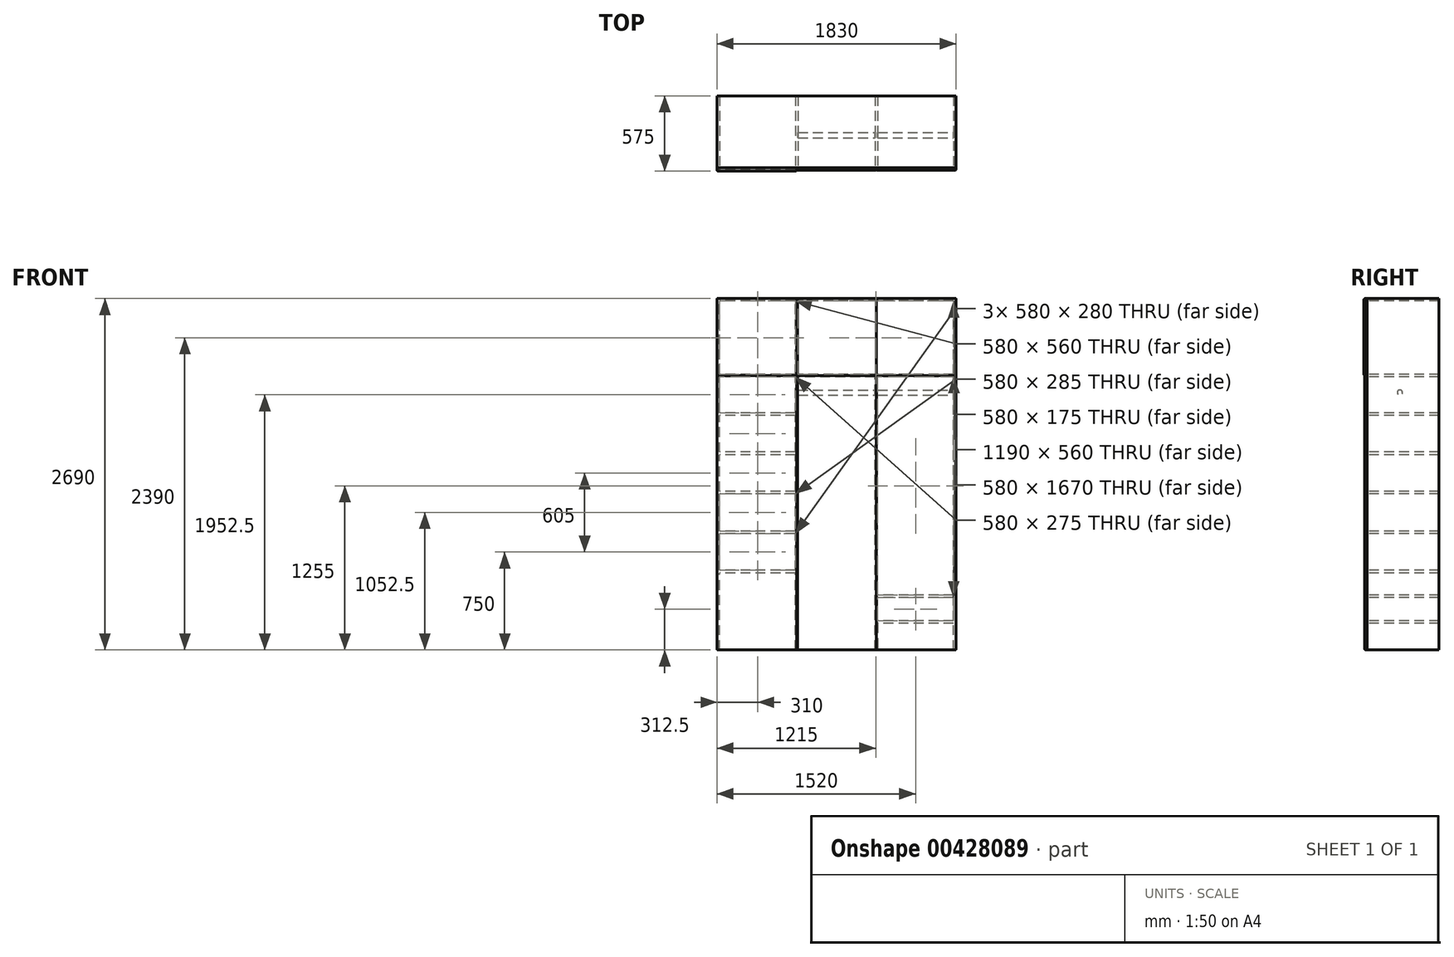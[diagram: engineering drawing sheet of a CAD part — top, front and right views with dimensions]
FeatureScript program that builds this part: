
annotation { "Feature Type Name" : "Feature", "Feature Type Description" : "" }
export const myFeature = defineFeature(function(context is Context, id is Id, definition is map)
    precondition{}
    {
        {
            var Q0;
            Q0=qCreatedBy(makeId("Front.planeOp"),FACE);
            var sketch = newSketch(context, id + "F0", { "sketchPlane" : qUnion([Q0])});
            skLineSegment(sketch, "E0.bottom", {"start": v(915, -1345) * mm, "end": v(-915, -1345) * mm});
            skLineSegment(sketch, "E0.top", {"start": v(915, 1345) * mm, "end": v(-915, 1345) * mm});
            skLineSegment(sketch, "E0.left", {"start": v(915, -1345) * mm, "end": v(915, 1345) * mm});
            skLineSegment(sketch, "E0.right", {"start": v(-915, -1345) * mm, "end": v(-915, 1345) * mm});
            skPoint(sketch, "E0.middle", {"position": v(0, 0) * mm});
            skLineSegment(sketch, "E1.0", {"start": v(895, 745) * mm, "end": v(315, 745) * mm});
            skLineSegment(sketch, "E2.trimOffspring", {"start": v(-315, 745) * mm, "end": v(-895, 745) * mm});
            skLineSegment(sketch, "E3", {"start": v(295, 745) * mm, "end": v(-295, 745) * mm});
            skLineSegment(sketch, "E4.0", {"start": v(-315, 470) * mm, "end": v(-895, 470) * mm});
            skLineSegment(sketch, "E5.0", {"start": v(-315, 170) * mm, "end": v(-895, 170) * mm});
            skLineSegment(sketch, "E6.0", {"start": v(-315, -130) * mm, "end": v(-895, -130) * mm});
            skLineSegment(sketch, "E7.0", {"start": v(-315, -455) * mm, "end": v(-895, -455) * mm});
            skLineSegment(sketch, "E8.0", {"start": v(-315, -755) * mm, "end": v(-895, -755) * mm});
            skLineSegment(sketch, "E9.0", {"start": v(895, -945) * mm, "end": v(315, -945) * mm});
            skLineSegment(sketch, "E10.0", {"start": v(295, 645) * mm, "end": v(-295, 645) * mm});
            skLineSegment(sketch, "E11.0", {"start": v(295, 625) * mm, "end": v(-295, 625) * mm});
            skLineSegment(sketch, "E12.0", {"start": v(295, -375) * mm, "end": v(-295, -375) * mm});
            skLineSegment(sketch, "E13.0", {"start": v(295, -395) * mm, "end": v(-295, -395) * mm});
            skLineSegment(sketch, "E14", {"start": v(315, 645) * mm, "end": v(895, 645) * mm});
            skLineSegment(sketch, "E15", {"start": v(315, 625) * mm, "end": v(895, 625) * mm});
            skLineSegment(sketch, "E16.0", {"start": v(895, -1120) * mm, "end": v(315, -1120) * mm});
            skLineSegment(sketch, "E17.0", {"start": v(-895, -1345) * mm, "end": v(-895, -755) * mm});
            skLineSegment(sketch, "E18.0", {"start": v(895, 1325) * mm, "end": v(-295, 1325) * mm});
            skLineSegment(sketch, "E19.0", {"start": v(895, -1320) * mm, "end": v(895, -1140) * mm});
            skLineSegment(sketch, "E20.0", {"start": v(-315, 765) * mm, "end": v(-895, 765) * mm});
            skLineSegment(sketch, "E20.1", {"start": v(295, 765) * mm, "end": v(-295, 765) * mm});
            skLineSegment(sketch, "E20.2", {"start": v(895, 765) * mm, "end": v(315, 765) * mm});
            skLineSegment(sketch, "E21.0", {"start": v(-315, 450) * mm, "end": v(-895, 450) * mm});
            skLineSegment(sketch, "E22.0", {"start": v(-315, 150) * mm, "end": v(-895, 150) * mm});
            skLineSegment(sketch, "E23.0", {"start": v(-315, -150) * mm, "end": v(-895, -150) * mm});
            skLineSegment(sketch, "E24.0", {"start": v(-315, -435) * mm, "end": v(-895, -435) * mm});
            skLineSegment(sketch, "E25.0", {"start": v(-315, -735) * mm, "end": v(-895, -735) * mm});
            skLineSegment(sketch, "E26.0", {"start": v(895, -925) * mm, "end": v(315, -925) * mm});
            skLineSegment(sketch, "E27.0", {"start": v(895, -1140) * mm, "end": v(315, -1140) * mm});
            skLineSegment(sketch, "E28.0", {"start": v(295, -1345) * mm, "end": v(295, 745) * mm});
            skLineSegment(sketch, "E29.0", {"start": v(315, -1320) * mm, "end": v(315, -1140) * mm});
            skLineSegment(sketch, "E30.0", {"start": v(-295, -1345) * mm, "end": v(-295, 745) * mm});
            skLineSegment(sketch, "E31.0", {"start": v(-315, -1345) * mm, "end": v(-315, -755) * mm});
            skLineSegment(sketch, "E32.trimOffspring", {"start": v(-315, 1325) * mm, "end": v(-895, 1325) * mm});
            skLineSegment(sketch, "E33.trimOffspring", {"start": v(895, 765) * mm, "end": v(895, 1325) * mm});
            skLineSegment(sketch, "E34.trimOffspring", {"start": v(-295, 765) * mm, "end": v(-295, 1325) * mm});
            skLineSegment(sketch, "E35.trimOffspring", {"start": v(-315, 765) * mm, "end": v(-315, 1325) * mm});
            skLineSegment(sketch, "E36.trimOffspring", {"start": v(-895, 765) * mm, "end": v(-895, 1325) * mm});
            skLineSegment(sketch, "E37.trimOffspring", {"start": v(-895, 470) * mm, "end": v(-895, 745) * mm});
            skLineSegment(sketch, "E38.trimOffspring", {"start": v(-315, 470) * mm, "end": v(-315, 745) * mm});
            skLineSegment(sketch, "E39.trimOffspring", {"start": v(-895, 170) * mm, "end": v(-895, 450) * mm});
            skLineSegment(sketch, "E40.trimOffspring", {"start": v(-895, -130) * mm, "end": v(-895, 150) * mm});
            skLineSegment(sketch, "E41.trimOffspring", {"start": v(-315, -130) * mm, "end": v(-315, 150) * mm});
            skLineSegment(sketch, "E42.trimOffspring", {"start": v(-315, 170) * mm, "end": v(-315, 450) * mm});
            skLineSegment(sketch, "E43.trimOffspring", {"start": v(-315, -435) * mm, "end": v(-315, -150) * mm});
            skLineSegment(sketch, "E44.trimOffspring", {"start": v(-895, -435) * mm, "end": v(-895, -150) * mm});
            skLineSegment(sketch, "E45.trimOffspring", {"start": v(-895, -735) * mm, "end": v(-895, -455) * mm});
            skPoint(sketch, "E46.orphan", {"position": v(-915, -755) * mm});
            skLineSegment(sketch, "E47.trimOffspring", {"start": v(-315, -735) * mm, "end": v(-315, -455) * mm});
            skLineSegment(sketch, "E48.trimOffspring", {"start": v(315, -925) * mm, "end": v(315, 745) * mm});
            skLineSegment(sketch, "E49.trimOffspring", {"start": v(895, -925) * mm, "end": v(895, 745) * mm});
            skPoint(sketch, "E50.orphan", {"position": v(915, -945) * mm});
            skLineSegment(sketch, "E51.trimOffspring", {"start": v(895, -1120) * mm, "end": v(895, -945) * mm});
            skLineSegment(sketch, "E52.trimOffspring", {"start": v(315, -1120) * mm, "end": v(315, -945) * mm});
            skLineSegment(sketch, "E53", {"start": v(315, 765) * mm, "end": v(295, 765) * mm});
            skLineSegment(sketch, "E54", {"start": v(315, -1320) * mm, "end": v(315, -1345) * mm});
            skLineSegment(sketch, "E55", {"start": v(895, -1320) * mm, "end": v(895, -1345) * mm});
            skSolve(sketch);
        }
        {
            var Q0;
            Q0=makeQuery(id+"F0.imprint","IMPRINT",FACE,{"disambiguationData":[TD([[makeQuery(id+"F0.imprint","IMPRINT",EDGE,{"derivedFrom":sQuery(id+"F0.wireOp",EDGE,"E0.top")}),1.0]])]});
            extrude(context, id + "F1", {"entities" : qUnion([Q0]), "oppositeDirection" : true, "depth" : 550 * mm});
        }
        {
            var Q0;
            {var subQ0=sQuery(id+"F0.wireOp",EDGE,"E10.0");Q0=makeQuery(id+"F0.imprint","IMPRINT",FACE,{"disambiguationData":[TD([[makeQuery(id+"F0.imprint","IMPRINT",EDGE,{"derivedFrom":subQ0}),1.0]])]});}
            var Q1;
            {var subQ0=sQuery(id+"F0.wireOp",EDGE,"E14");Q1=makeQuery(id+"F0.imprint","IMPRINT",FACE,{"disambiguationData":[TD([[makeQuery(id+"F0.imprint","IMPRINT",EDGE,{"derivedFrom":subQ0}),-1.0]])]});}
            var Q2;
            Q2=sQuery(id+"F0.wireOp",EDGE,"E11.0");
            revolve(context, id + "F2", {"entities" : qUnion([Q0, Q1]), "axis" : qUnion([Q2]), "revolveType" : RevolveType.FULL});
        }
        {
            var Q0;
            Q0=sQuery(id+"F0.wireOp",EDGE,"E12.0");
            var Q1;
            Q1=sQuery(id+"F0.wireOp",EDGE,"E13.0");
            revolve(context, id + "F3", {"bodyType" : ToolBodyType.SURFACE, "surfaceEntities" : qUnion([Q0]), "axis" : qUnion([Q1]), "revolveType" : RevolveType.FULL});
        }
        {
            var Q0;
            Q0=makeQuery(id+"F2.opRevolve","SWEPT_BODY",BODY,{"disambiguationData":[OSD([sQuery(id+"F0.wireOp",EDGE,"E10.0"),sQuery(id+"F0.wireOp",EDGE,"E11.0"),sQuery(id+"F0.wireOp",EDGE,"E28.0"),sQuery(id+"F0.wireOp",EDGE,"E30.0")])]});
            var Q1;
            Q1=makeQuery(id+"F2.opRevolve","SWEPT_BODY",BODY,{"disambiguationData":[OSD([sQuery(id+"F0.wireOp",EDGE,"E14"),sQuery(id+"F0.wireOp",EDGE,"E15"),sQuery(id+"F0.wireOp",EDGE,"E48.trimOffspring"),sQuery(id+"F0.wireOp",EDGE,"E49.trimOffspring")])]});
            var Q2;
            Q2=makeQuery(id+"F3.opRevolve","SWEPT_BODY",BODY,{"disambiguationData":[OSD([sQuery(id+"F0.wireOp",EDGE,"E12.0")])]});
            var Q3;
            Q3=makeQuery(id+"F1.opExtrude","SWEPT_EDGE",EDGE,{"disambiguationData":[OSD([sQuery(id+"F0.wireOp",EDGE,"E25.0"),sQuery(id+"F0.wireOp",EDGE,"E45.trimOffspring")])]});
            transform(context, id + "F4", {"entities" : qUnion([Q0, Q1, Q2]), "transformType" : TransformType.TRANSLATION_DISTANCE, "transformDirection" : qUnion([Q3]), "distance" : 250 * mm, "oppositeDirection" : true, "makeCopy" : false});
        }
        {
            var Q0;
            Q0=qCreatedBy(makeId("Front.planeOp"),FACE);
            var sketch = newSketch(context, id + "F5", { "sketchPlane" : qUnion([Q0])});
            skLineSegment(sketch, "E56.bottom", {"start": v(915, -1345) * mm, "end": v(-915, -1345) * mm});
            skLineSegment(sketch, "E56.top", {"start": v(915, 1345) * mm, "end": v(-915, 1345) * mm});
            skLineSegment(sketch, "E56.left", {"start": v(915, -1345) * mm, "end": v(915, 1345) * mm});
            skLineSegment(sketch, "E56.right", {"start": v(-915, -1345) * mm, "end": v(-915, 1345) * mm});
            skPoint(sketch, "E56.middle", {"position": v(0, 0) * mm});
            skLineSegment(sketch, "E57.0", {"start": v(305, -1345) * mm, "end": v(305, 1345) * mm});
            skLineSegment(sketch, "E58.0", {"start": v(-305, -1345) * mm, "end": v(-305, 1345) * mm});
            skLineSegment(sketch, "E59.0", {"start": v(-300, -1345) * mm, "end": v(-300, 1345) * mm});
            skLineSegment(sketch, "E60.0", {"start": v(915, 755) * mm, "end": v(-915, 755) * mm});
            skSolve(sketch);
        }
        {
            var Q0;
            {var subQ0=sQuery(id+"F5.wireOp",EDGE,"E56.right");var subQ1=sQuery(id+"F5.wireOp",EDGE,"E56.bottom");var subQ2=makeQuery(id+"F5.imprint","INTERSECT",VERTEX,{"derivedFrom":[subQ1,subQ0]});Q0=makeQuery(id+"F5.imprint","IMPRINT",FACE,{"disambiguationData":[TD([[makeQuery(id+"F5.imprint","IMPRINT",EDGE,{"disambiguationData":[TD([[subQ2,1.0]])],"derivedFrom":subQ1}),-1.0]])]});}
            extrude(context, id + "F6", {"entities" : qUnion([Q0]), "depth" : 20 * mm});
        }
        {
            var Q0;
            Q0=makeQuery(id+"F6.opExtrude","SWEPT_EDGE",EDGE,{"disambiguationData":[OSD([sQuery(id+"F5.wireOp",EDGE,"E58.0"),sQuery(id+"F5.wireOp",EDGE,"E60.0")])]});
            var Q1;
            Q1=makeQuery(id+"F6.opExtrude","SWEPT_EDGE",EDGE,{"disambiguationData":[OSD([sQuery(id+"F5.wireOp",EDGE,"E56.right"),sQuery(id+"F5.wireOp",EDGE,"E60.0")])]});
            var Q2;
            Q2=makeQuery(id+"F6.opExtrude","SWEPT_EDGE",EDGE,{"disambiguationData":[OSD([sQuery(id+"F5.wireOp",EDGE,"E56.bottom"),sQuery(id+"F5.wireOp",EDGE,"E56.right")])]});
            var Q3;
            Q3=makeQuery(id+"F6.opExtrude","SWEPT_EDGE",EDGE,{"disambiguationData":[OSD([sQuery(id+"F5.wireOp",EDGE,"E56.bottom"),sQuery(id+"F5.wireOp",EDGE,"E58.0")])]});
            var Q4;
            Q4=makeQuery(id+"F6.opExtrude","CAP_FACE",FACE,{"disambiguationData":[OSD([sQuery(id+"F5.wireOp",EDGE,"E56.bottom"),sQuery(id+"F5.wireOp",EDGE,"E56.right"),sQuery(id+"F5.wireOp",EDGE,"E58.0"),sQuery(id+"F5.wireOp",EDGE,"E60.0")])],"isStart":false});
            fillet(context, id + "F7", {"entities" : qUnion([Q0, Q1, Q2, Q3, Q4]), "radius" : 10 * mm, "tangentPropagation" : true, "allowEdgeOverflow" : false});
        }
        {
            var Q0;
            {var subQ0=sQuery(id+"F5.wireOp",EDGE,"E57.0");var subQ1=sQuery(id+"F5.wireOp",EDGE,"E56.bottom");var subQ2=makeQuery(id+"F5.imprint","INTERSECT",VERTEX,{"derivedFrom":[subQ1,subQ0]});Q0=makeQuery(id+"F5.imprint","IMPRINT",FACE,{"disambiguationData":[TD([[makeQuery(id+"F5.imprint","IMPRINT",EDGE,{"disambiguationData":[TD([[subQ2,-1.0]])],"derivedFrom":subQ1}),-1.0]])]});}
            extrude(context, id + "F8", {"entities" : qUnion([Q0]), "depth" : 20 * mm});
        }
        {
            var Q0;
            Q0=makeQuery(id+"F8.opExtrude","CAP_FACE",FACE,{"disambiguationData":[OSD([sQuery(id+"F5.wireOp",EDGE,"E56.bottom"),sQuery(id+"F5.wireOp",EDGE,"E57.0"),sQuery(id+"F5.wireOp",EDGE,"E59.0"),sQuery(id+"F5.wireOp",EDGE,"E60.0")])],"isStart":false});
            var Q1;
            Q1=makeQuery(id+"F8.opExtrude","SWEPT_EDGE",EDGE,{"disambiguationData":[OSD([sQuery(id+"F5.wireOp",EDGE,"E57.0"),sQuery(id+"F5.wireOp",EDGE,"E60.0")])]});
            var Q2;
            Q2=makeQuery(id+"F8.opExtrude","SWEPT_EDGE",EDGE,{"disambiguationData":[OSD([sQuery(id+"F5.wireOp",EDGE,"E59.0"),sQuery(id+"F5.wireOp",EDGE,"E60.0")])]});
            var Q3;
            Q3=makeQuery(id+"F8.opExtrude","SWEPT_EDGE",EDGE,{"disambiguationData":[OSD([sQuery(id+"F5.wireOp",EDGE,"E56.bottom"),sQuery(id+"F5.wireOp",EDGE,"E57.0")])]});
            var Q4;
            Q4=makeQuery(id+"F8.opExtrude","SWEPT_EDGE",EDGE,{"disambiguationData":[OSD([sQuery(id+"F5.wireOp",EDGE,"E56.bottom"),sQuery(id+"F5.wireOp",EDGE,"E59.0")])]});
            fillet(context, id + "F9", {"entities" : qUnion([Q0, Q1, Q2, Q3, Q4]), "radius" : 10 * mm, "tangentPropagation" : true, "allowEdgeOverflow" : false});
        }
        {
            var Q0;
            {var subQ0=sQuery(id+"F5.wireOp",EDGE,"E56.left");var subQ1=sQuery(id+"F5.wireOp",EDGE,"E56.bottom");var subQ2=makeQuery(id+"F5.imprint","INTERSECT",VERTEX,{"derivedFrom":[subQ1,subQ0]});Q0=makeQuery(id+"F5.imprint","IMPRINT",FACE,{"disambiguationData":[TD([[makeQuery(id+"F5.imprint","IMPRINT",EDGE,{"disambiguationData":[TD([[subQ2,-1.0]])],"derivedFrom":subQ1}),-1.0]])]});}
            extrude(context, id + "F10", {"entities" : qUnion([Q0]), "depth" : 20 * mm});
        }
        {
            var Q0;
            Q0=makeQuery(id+"F10.opExtrude","CAP_FACE",FACE,{"disambiguationData":[OSD([sQuery(id+"F5.wireOp",EDGE,"E56.bottom"),sQuery(id+"F5.wireOp",EDGE,"E56.left"),sQuery(id+"F5.wireOp",EDGE,"E57.0"),sQuery(id+"F5.wireOp",EDGE,"E60.0")])],"isStart":false});
            var Q1;
            Q1=makeQuery(id+"F10.opExtrude","SWEPT_EDGE",EDGE,{"disambiguationData":[OSD([sQuery(id+"F5.wireOp",EDGE,"E56.left"),sQuery(id+"F5.wireOp",EDGE,"E60.0")])]});
            var Q2;
            Q2=makeQuery(id+"F10.opExtrude","SWEPT_EDGE",EDGE,{"disambiguationData":[OSD([sQuery(id+"F5.wireOp",EDGE,"E57.0"),sQuery(id+"F5.wireOp",EDGE,"E60.0")])]});
            var Q3;
            Q3=makeQuery(id+"F10.opExtrude","SWEPT_EDGE",EDGE,{"disambiguationData":[OSD([sQuery(id+"F5.wireOp",EDGE,"E56.bottom"),sQuery(id+"F5.wireOp",EDGE,"E57.0")])]});
            var Q4;
            Q4=makeQuery(id+"F10.opExtrude","SWEPT_EDGE",EDGE,{"disambiguationData":[OSD([sQuery(id+"F5.wireOp",EDGE,"E56.bottom"),sQuery(id+"F5.wireOp",EDGE,"E56.left")])]});
            fillet(context, id + "F11", {"entities" : qUnion([Q0, Q1, Q2, Q3, Q4]), "radius" : 10 * mm, "tangentPropagation" : true, "allowEdgeOverflow" : false});
        }
        {
            var Q0;
            {var subQ0=sQuery(id+"F5.wireOp",EDGE,"E56.left");var subQ1=sQuery(id+"F5.wireOp",EDGE,"E56.top");var subQ2=makeQuery(id+"F5.imprint","INTERSECT",VERTEX,{"derivedFrom":[subQ1,subQ0]});Q0=makeQuery(id+"F5.imprint","IMPRINT",FACE,{"disambiguationData":[TD([[makeQuery(id+"F5.imprint","IMPRINT",EDGE,{"disambiguationData":[TD([[subQ2,-1.0]])],"derivedFrom":subQ1}),1.0]])]});}
            extrude(context, id + "F12", {"entities" : qUnion([Q0]), "depth" : 20 * mm});
        }
        {
            var Q0;
            Q0=makeQuery(id+"F12.opExtrude","CAP_FACE",FACE,{"disambiguationData":[OSD([sQuery(id+"F5.wireOp",EDGE,"E56.top"),sQuery(id+"F5.wireOp",EDGE,"E56.left"),sQuery(id+"F5.wireOp",EDGE,"E57.0"),sQuery(id+"F5.wireOp",EDGE,"E60.0")])],"isStart":false});
            var Q1;
            Q1=makeQuery(id+"F12.opExtrude","SWEPT_EDGE",EDGE,{"disambiguationData":[OSD([sQuery(id+"F5.wireOp",EDGE,"E56.top"),sQuery(id+"F5.wireOp",EDGE,"E56.left")])]});
            var Q2;
            Q2=makeQuery(id+"F12.opExtrude","SWEPT_EDGE",EDGE,{"disambiguationData":[OSD([sQuery(id+"F5.wireOp",EDGE,"E56.left"),sQuery(id+"F5.wireOp",EDGE,"E60.0")])]});
            var Q3;
            Q3=makeQuery(id+"F12.opExtrude","SWEPT_EDGE",EDGE,{"disambiguationData":[OSD([sQuery(id+"F5.wireOp",EDGE,"E56.top"),sQuery(id+"F5.wireOp",EDGE,"E57.0")])]});
            var Q4;
            Q4=makeQuery(id+"F12.opExtrude","SWEPT_EDGE",EDGE,{"disambiguationData":[OSD([sQuery(id+"F5.wireOp",EDGE,"E57.0"),sQuery(id+"F5.wireOp",EDGE,"E60.0")])]});
            fillet(context, id + "F13", {"entities" : qUnion([Q0, Q1, Q2, Q3, Q4]), "radius" : 10 * mm, "tangentPropagation" : true, "allowEdgeOverflow" : false});
        }
        {
            var Q0;
            {var subQ0=sQuery(id+"F5.wireOp",EDGE,"E57.0");var subQ1=sQuery(id+"F5.wireOp",EDGE,"E56.top");var subQ2=makeQuery(id+"F5.imprint","INTERSECT",VERTEX,{"derivedFrom":[subQ1,subQ0]});Q0=makeQuery(id+"F5.imprint","IMPRINT",FACE,{"disambiguationData":[TD([[makeQuery(id+"F5.imprint","IMPRINT",EDGE,{"disambiguationData":[TD([[subQ2,-1.0]])],"derivedFrom":subQ1}),1.0]])]});}
            extrude(context, id + "F14", {"entities" : qUnion([Q0]), "depth" : 20 * mm});
        }
        {
            var Q0;
            Q0=makeQuery(id+"F14.opExtrude","CAP_FACE",FACE,{"disambiguationData":[OSD([sQuery(id+"F5.wireOp",EDGE,"E56.top"),sQuery(id+"F5.wireOp",EDGE,"E57.0"),sQuery(id+"F5.wireOp",EDGE,"E59.0"),sQuery(id+"F5.wireOp",EDGE,"E60.0")])],"isStart":false});
            var Q1;
            Q1=makeQuery(id+"F14.opExtrude","SWEPT_EDGE",EDGE,{"disambiguationData":[OSD([sQuery(id+"F5.wireOp",EDGE,"E56.top"),sQuery(id+"F5.wireOp",EDGE,"E59.0")])]});
            var Q2;
            Q2=makeQuery(id+"F14.opExtrude","SWEPT_EDGE",EDGE,{"disambiguationData":[OSD([sQuery(id+"F5.wireOp",EDGE,"E56.top"),sQuery(id+"F5.wireOp",EDGE,"E57.0")])]});
            var Q3;
            Q3=makeQuery(id+"F14.opExtrude","SWEPT_EDGE",EDGE,{"disambiguationData":[OSD([sQuery(id+"F5.wireOp",EDGE,"E57.0"),sQuery(id+"F5.wireOp",EDGE,"E60.0")])]});
            var Q4;
            Q4=makeQuery(id+"F14.opExtrude","SWEPT_EDGE",EDGE,{"disambiguationData":[OSD([sQuery(id+"F5.wireOp",EDGE,"E59.0"),sQuery(id+"F5.wireOp",EDGE,"E60.0")])]});
            fillet(context, id + "F15", {"entities" : qUnion([Q0, Q1, Q2, Q3, Q4]), "radius" : 10 * mm, "tangentPropagation" : true, "allowEdgeOverflow" : false});
        }
        {
            var Q0;
            {var subQ0=sQuery(id+"F5.wireOp",EDGE,"E56.right");var subQ1=sQuery(id+"F5.wireOp",EDGE,"E56.top");var subQ2=makeQuery(id+"F5.imprint","INTERSECT",VERTEX,{"derivedFrom":[subQ1,subQ0]});Q0=makeQuery(id+"F5.imprint","IMPRINT",FACE,{"disambiguationData":[TD([[makeQuery(id+"F5.imprint","IMPRINT",EDGE,{"disambiguationData":[TD([[subQ2,1.0]])],"derivedFrom":subQ1}),1.0]])]});}
            extrude(context, id + "F16", {"entities" : qUnion([Q0]), "depth" : 25 * mm});
        }
        {
            var Q0;
            Q0=makeQuery(id+"F16.opExtrude","CAP_FACE",FACE,{"disambiguationData":[OSD([sQuery(id+"F5.wireOp",EDGE,"E56.top"),sQuery(id+"F5.wireOp",EDGE,"E56.right"),sQuery(id+"F5.wireOp",EDGE,"E58.0"),sQuery(id+"F5.wireOp",EDGE,"E60.0")])],"isStart":false});
            var Q1;
            Q1=makeQuery(id+"F16.opExtrude","SWEPT_EDGE",EDGE,{"disambiguationData":[OSD([sQuery(id+"F5.wireOp",EDGE,"E56.top"),sQuery(id+"F5.wireOp",EDGE,"E56.right")])]});
            var Q2;
            Q2=makeQuery(id+"F16.opExtrude","SWEPT_EDGE",EDGE,{"disambiguationData":[OSD([sQuery(id+"F5.wireOp",EDGE,"E56.top"),sQuery(id+"F5.wireOp",EDGE,"E58.0")])]});
            var Q3;
            Q3=makeQuery(id+"F16.opExtrude","SWEPT_EDGE",EDGE,{"disambiguationData":[OSD([sQuery(id+"F5.wireOp",EDGE,"E56.right"),sQuery(id+"F5.wireOp",EDGE,"E60.0")])]});
            var Q4;
            Q4=makeQuery(id+"F16.opExtrude","SWEPT_EDGE",EDGE,{"disambiguationData":[OSD([sQuery(id+"F5.wireOp",EDGE,"E58.0"),sQuery(id+"F5.wireOp",EDGE,"E60.0")])]});
            fillet(context, id + "F17", {"entities" : qUnion([Q0, Q1, Q2, Q3, Q4]), "radius" : 10 * mm, "tangentPropagation" : true, "allowEdgeOverflow" : false});
        }
    });
